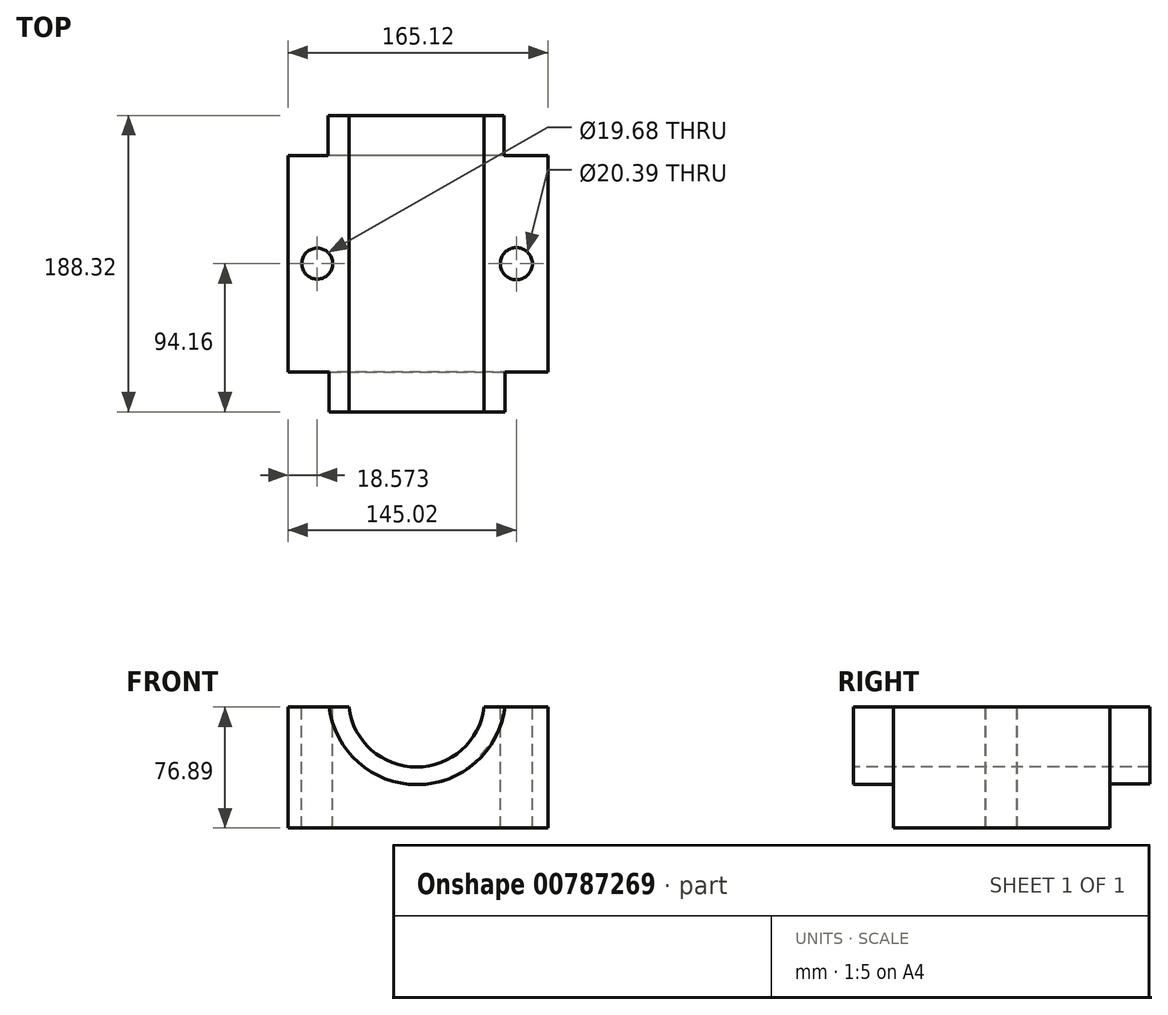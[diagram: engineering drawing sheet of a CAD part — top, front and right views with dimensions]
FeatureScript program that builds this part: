
annotation { "Feature Type Name" : "Feature", "Feature Type Description" : "" }
export const myFeature = defineFeature(function(context is Context, id is Id, definition is map)
    precondition{}
    {
        {
            var Q0;
            Q0=qCreatedBy(makeId("Top.planeOp"),FACE);
            var sketch = newSketch(context, id + "F0", { "sketchPlane" : qUnion([Q0])});
            skLineSegment(sketch, "E0.bottom", {"start": v(69.86, -68.76) * mm, "end": v(-69.86, -68.76) * mm});
            skLineSegment(sketch, "E0.top", {"start": v(69.86, 68.76) * mm, "end": v(-69.86, 68.76) * mm});
            skLineSegment(sketch, "E0.left", {"start": v(69.86, -68.76) * mm, "end": v(69.86, 68.76) * mm});
            skLineSegment(sketch, "E0.right", {"start": v(-69.86, -68.76) * mm, "end": v(-69.86, 68.76) * mm});
            skPoint(sketch, "E0.middle", {"position": v(0, 0) * mm});
            skLineSegment(sketch, "E1", {"start": v(0, 68.76) * mm, "end": v(0, -68.76) * mm});
            skSolve(sketch);
        }
        {
            var Q0;
            {var subQ0=sQuery(id+"F0.wireOp",EDGE,"E0.right");Q0=makeQuery(id+"F0.imprint","IMPRINT",FACE,{"disambiguationData":[TD([[makeQuery(id+"F0.imprint","IMPRINT",EDGE,{"derivedFrom":subQ0}),-1.0]])]});}
            var Q1;
            {var subQ0=sQuery(id+"F0.wireOp",EDGE,"E0.left");Q1=makeQuery(id+"F0.imprint","IMPRINT",FACE,{"disambiguationData":[TD([[makeQuery(id+"F0.imprint","IMPRINT",EDGE,{"derivedFrom":subQ0}),1.0]])]});}
            extrude(context, id + "F1", {"entities" : qUnion([Q0, Q1]), "oppositeDirection" : true, "depth" : 76.9 * mm});
        }
        {
            var Q0;
            Q0=makeQuery(id+"F1.opExtrude","SWEPT_FACE",FACE,{"disambiguationData":[OSD([sQuery(id+"F0.wireOp",EDGE,"E0.right")])]});
            extrude(context, id + "F2", {"entities" : qUnion([Q0]), "operationType" : NewBodyOperationType.ADD, "oppositeDirection" : true, "depth" : 25.4 * mm, "offsetDistance" : 25.4 * mm});
        }
        {
            var Q0;
            Q0=makeQuery(id+"F1.opExtrude","SWEPT_FACE",FACE,{"disambiguationData":[OSD([sQuery(id+"F0.wireOp",EDGE,"E0.right")])]});
            extrude(context, id + "F3", {"entities" : qUnion([Q0]), "operationType" : NewBodyOperationType.ADD, "depth" : 25.4 * mm, "offsetDistance" : 25.4 * mm});
        }
        {
            var Q0;
            {var subQ0=sQuery(id+"F0.wireOp",EDGE,"E0.bottom");Q0=makeQuery(id+"F3.boolean.opBoolean","MERGE",FACE,{"derivedFrom":[makeQuery(id+"F1.opExtrude","SWEPT_FACE",FACE,{"disambiguationData":[OSD([subQ0])]}),makeQuery(id+"F3.opExtrude","SWEPT_FACE",FACE,{"disambiguationData":[OSD([subQ0,sQuery(id+"F0.wireOp",EDGE,"E0.right")])]})]});}
            var sketch = newSketch(context, id + "F4", { "sketchPlane" : qUnion([Q0])});
            skArc(sketch, "E2", {"start": v(-69.2, 0) * mm, "mid": v(-13.28, -49.23) * mm, "end": v(42.64, 0) * mm});
            skArc(sketch, "E3", {"start": v(-56.62, 0) * mm, "mid": v(-13.65, -38.13) * mm, "end": v(29.32, 0) * mm});
            skSolve(sketch);
        }
        {
            var Q0;
            {var subQ0=sQuery(id+"F4.wireOp",EDGE,"E3");Q0=makeQuery(id+"F4.imprint","IMPRINT",FACE,{"disambiguationData":[TD([[makeQuery(id+"F4.imprint","IMPRINT",EDGE,{"derivedFrom":subQ0}),1.0]])]});}
            extrude(context, id + "F5", {"entities" : qUnion([Q0]), "operationType" : NewBodyOperationType.REMOVE, "oppositeDirection" : true, "depth" : 1676.4 * mm, "offsetDistance" : 25.4 * mm});
        }
        {
            var Q0;
            {var subQ0=sQuery(id+"F4.wireOp",EDGE,"E2");Q0=makeQuery(id+"F4.imprint","IMPRINT",FACE,{"disambiguationData":[TD([[makeQuery(id+"F4.imprint","IMPRINT",EDGE,{"derivedFrom":subQ0}),1.0]])]});}
            extrude(context, id + "F6", {"entities" : qUnion([Q0]), "operationType" : NewBodyOperationType.ADD, "depth" : 25.4 * mm, "offsetDistance" : 25.4 * mm});
        }
        {
            var Q0;
            {var subQ0=sQuery(id+"F0.wireOp",EDGE,"E0.top");Q0=makeQuery(id+"F3.boolean.opBoolean","MERGE",FACE,{"derivedFrom":[makeQuery(id+"F1.opExtrude","SWEPT_FACE",FACE,{"disambiguationData":[OSD([subQ0])]}),makeQuery(id+"F3.opExtrude","SWEPT_FACE",FACE,{"disambiguationData":[OSD([subQ0,sQuery(id+"F0.wireOp",EDGE,"E0.right")])]})]});}
            var sketch = newSketch(context, id + "F7", { "sketchPlane" : qUnion([Q0])});
            skArc(sketch, "E4", {"start": v(-41.91, 0) * mm, "mid": v(13.89, -48.72) * mm, "end": v(69.7, 0) * mm});
            skSolve(sketch);
        }
        {
            var Q0;
            {var subQ0=sQuery(id+"F7.wireOp",EDGE,"E4");Q0=makeQuery(id+"F7.imprint","IMPRINT",FACE,{"disambiguationData":[TD([[makeQuery(id+"F7.imprint","IMPRINT",EDGE,{"derivedFrom":subQ0}),1.0]])]});}
            extrude(context, id + "F8", {"entities" : qUnion([Q0]), "operationType" : NewBodyOperationType.ADD, "depth" : 25.4 * mm, "offsetDistance" : 25.4 * mm});
        }
        {
            var Q0;
            {var subQ0=sQuery(id+"F0.wireOp",EDGE,"E0.right");var subQ1=makeQuery(id+"F3.opExtrude","SWEPT_FACE",FACE,{"disambiguationData":[OSD([subQ0]),TDD([makeQuery(id+"F1.opExtrude","CAP_EDGE",EDGE,{"disambiguationData":[OSD([subQ0])],"isStart":true})])]});var subQ2=sQuery(id+"F0.wireOp",EDGE,"E0.top");var subQ4=makeQuery(id+"F3.opExtrude","CAP_FACE",FACE,{"disambiguationData":[OSD([subQ0])],"isStart":false});var subQ8=sQuery(id+"F0.wireOp",EDGE,"E0.bottom");var subQ9=makeQuery(id+"F1.opExtrude","CAP_FACE",FACE,{"disambiguationData":[OSD([subQ8,subQ2,sQuery(id+"F0.wireOp",EDGE,"E0.left"),subQ0])],"isStart":true});var subQ10=makeQuery(id+"F5.boolean.opBoolean","SPLIT",EDGE,{"disambiguationData":[TD([subQ4])],"derivedFrom":makeQuery(id+"F3.boolean.opBoolean","MERGE",EDGE,{"derivedFrom":[makeQuery(id+"F1.opExtrude","CAP_EDGE",EDGE,{"disambiguationData":[OSD([subQ2])],"isStart":true}),makeQuery(id+"F3.opExtrude","SWEPT_EDGE",EDGE,{"disambiguationData":[OSD([subQ2,subQ0]),TDD([makeQuery(id+"F1.opExtrude","CAP_VERTEX",VERTEX,{"disambiguationData":[OSD([subQ2,subQ0])],"isStart":true})])]})]})});var subQ11=makeQuery(id+"F3.boolean.opBoolean","MERGE",EDGE,{"derivedFrom":[makeQuery(id+"F1.opExtrude","CAP_EDGE",EDGE,{"disambiguationData":[OSD([subQ8])],"isStart":true}),makeQuery(id+"F3.opExtrude","SWEPT_EDGE",EDGE,{"disambiguationData":[OSD([subQ8,subQ0]),TDD([makeQuery(id+"F1.opExtrude","CAP_VERTEX",VERTEX,{"disambiguationData":[OSD([subQ8,subQ0])],"isStart":true})])]})]});Q0=makeQuery(id+"F8.boolean.opBoolean","MERGE",FACE,{"derivedFrom":[makeQuery(id+"F6.boolean.opBoolean","MERGE",FACE,{"derivedFrom":[makeQuery(id+"F5.boolean.opBoolean","SPLIT",FACE,{"disambiguationData":[TD([subQ4])],"derivedFrom":makeQuery(id+"F3.boolean.opBoolean","MERGE",FACE,{"derivedFrom":[subQ9,subQ1]})}),makeQuery(id+"F6.opExtrude","SWEPT_FACE",FACE,{"disambiguationData":[OSD([subQ8,subQ0]),TDD([makeQuery(id+"F4.imprint","IMPRINT",EDGE,{"disambiguationData":[TD([[makeQuery(id+"F4.imprint","INTERSECT",VERTEX,{"disambiguationData":[OD(0.0)],"derivedFrom":[subQ11,sQuery(id+"F4.wireOp",EDGE,"E2")]}),1.0]])],"derivedFrom":subQ11})])]})]}),makeQuery(id+"F8.opExtrude","SWEPT_FACE",FACE,{"disambiguationData":[OSD([subQ2,subQ0]),TDD([makeQuery(id+"F7.imprint","IMPRINT",EDGE,{"disambiguationData":[TD([[makeQuery(id+"F7.imprint","INTERSECT",VERTEX,{"derivedFrom":[subQ10,sQuery(id+"F7.wireOp",EDGE,"E4")]}),1.0]])],"derivedFrom":subQ10})])]})]});}
            var sketch = newSketch(context, id + "F9", { "sketchPlane" : qUnion([Q0])});
            skCircle(sketch, "E5", {"center": v(-76.69, 0) * mm, "radius": 9.84 * mm});
            skCircle(sketch, "E6", {"center": v(49.76, 0) * mm, "radius": 10.2 * mm});
            skSolve(sketch);
        }
        {
            var Q0;
            Q0=makeQuery(id+"F9.imprint","IMPRINT",FACE,{"disambiguationData":[TD([[makeQuery(id+"F9.imprint","IMPRINT",EDGE,{"derivedFrom":sQuery(id+"F9.wireOp",EDGE,"E5")}),1.0]])]});
            var Q1;
            Q1=makeQuery(id+"F9.imprint","IMPRINT",FACE,{"disambiguationData":[TD([[makeQuery(id+"F9.imprint","IMPRINT",EDGE,{"derivedFrom":sQuery(id+"F9.wireOp",EDGE,"E6")}),1.0]])]});
            extrude(context, id + "F10", {"entities" : qUnion([Q0, Q1]), "operationType" : NewBodyOperationType.REMOVE, "oppositeDirection" : true, "depth" : 2514.6 * mm, "offsetDistance" : 25.4 * mm});
        }
    });
